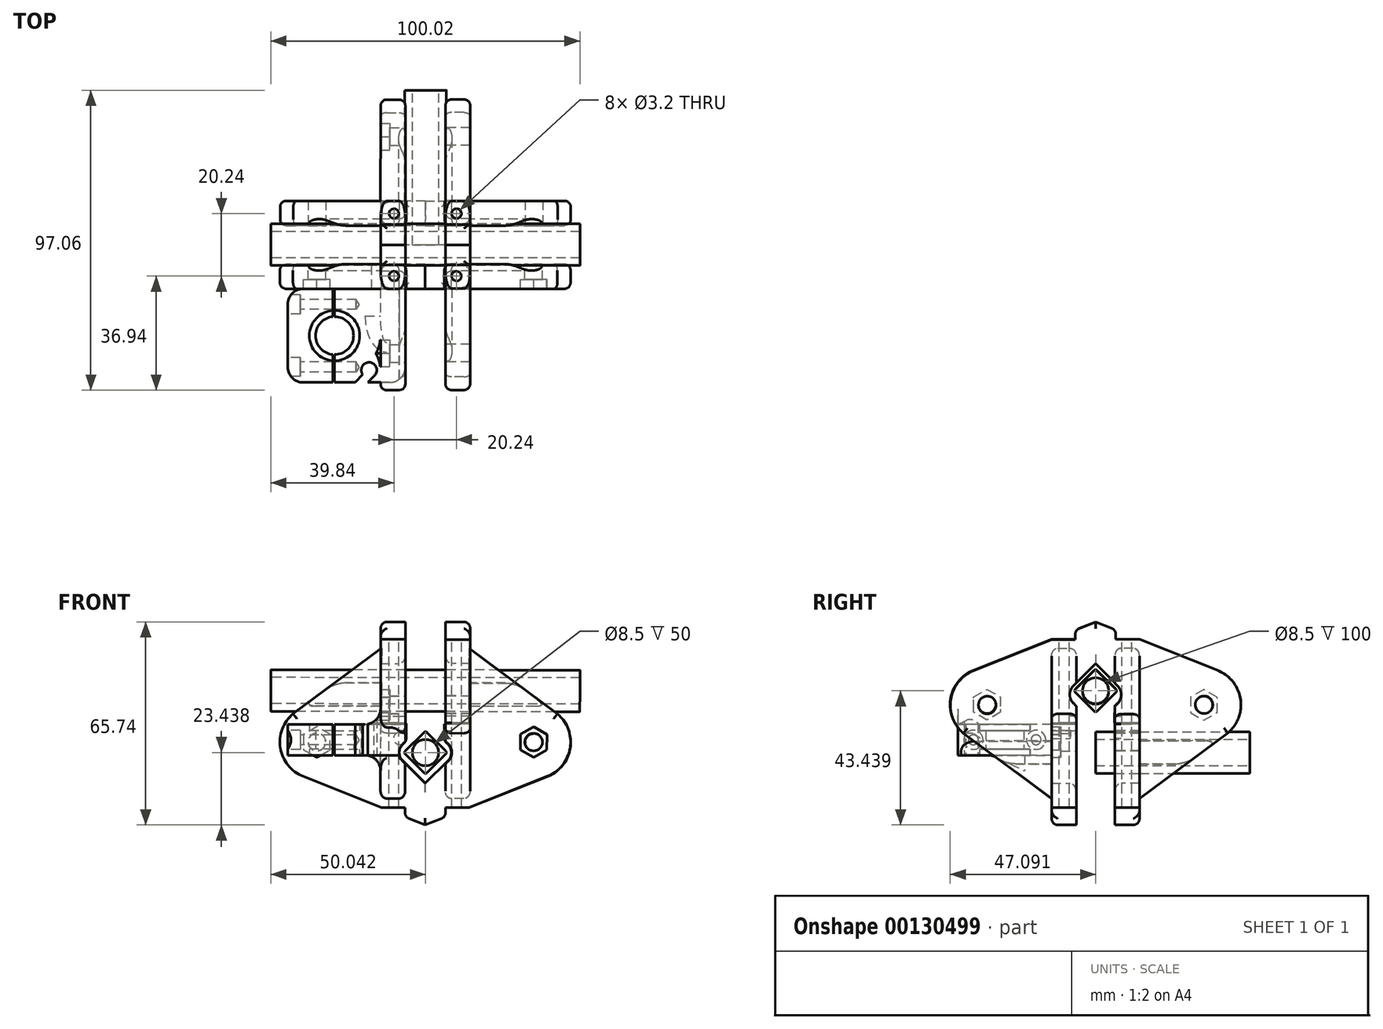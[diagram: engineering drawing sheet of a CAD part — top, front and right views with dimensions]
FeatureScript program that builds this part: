
annotation { "Feature Type Name" : "Feature", "Feature Type Description" : "" }
export const myFeature = defineFeature(function(context is Context, id is Id, definition is map)
    precondition{}
    {
        {
            assignVariable(context, id + "F0", {"name" : "wheelwidth", "anyValue" : 10.24});
        }
        {
            assignVariable(context, id + "F1", {"name" : "shimwidth", "anyValue" : 2});
        }
        {
            assignVariable(context, id + "F2", {"name" : "partwidth", "anyValue" : 8});
        }
        {
            var Q0;
            Q0=qCreatedBy(makeId("Front.planeOp"),FACE);
            var sketch = newSketch(context, id + "F3", { "sketchPlane" : qUnion([Q0])});
            skLineSegment(sketch, "E0.rect.bottom", {"start": v(6.59, -1.7) * mm, "end": v(0.65, -7.65) * mm});
            skLineSegment(sketch, "E0.rect.top", {"start": v(-0.48, 5.36) * mm, "end": v(-6.42, -0.58) * mm});
            skLineSegment(sketch, "E0.rect.left", {"start": v(6.59, -0.58) * mm, "end": v(0.65, 5.36) * mm});
            skLineSegment(sketch, "E0.rect.right", {"start": v(-0.48, -7.65) * mm, "end": v(-6.42, -1.7) * mm});
            skPoint(sketch, "E0.rect.middle", {"position": v(0.08, -1.14) * mm});
            skPoint(sketch, "E1.rect.middle", {"position": v(0.08, 18.86) * mm});
            skLineSegment(sketch, "E2", {"start": v(-6.66, 18.86) * mm, "end": v(6.82, 18.86) * mm, "construction": true});
            skCircle(sketch, "E3", {"center": v(35.08, 2.26) * mm, "radius": 11.95 * mm, "construction": true});
            skCircle(sketch, "E4", {"center": v(35.08, 2.26) * mm, "radius": 2.85 * mm});
            skCircle(sketch, "E5.cCircle", {"center": v(35.08, 2.26) * mm, "radius": 4.3 * mm, "construction": true});
            skLineSegment(sketch, "E5.0", {"start": v(39.39, 4.74) * mm, "end": v(39.38, -0.23) * mm});
            skLineSegment(sketch, "E5.1", {"start": v(39.38, -0.23) * mm, "end": v(35.08, -2.7) * mm});
            skLineSegment(sketch, "E5.2", {"start": v(35.08, -2.7) * mm, "end": v(30.78, -0.22) * mm});
            skLineSegment(sketch, "E5.3", {"start": v(30.78, -0.22) * mm, "end": v(30.79, 4.75) * mm});
            skLineSegment(sketch, "E5.4", {"start": v(30.79, 4.75) * mm, "end": v(35.09, 7.22) * mm});
            skLineSegment(sketch, "E5.5", {"start": v(35.09, 7.22) * mm, "end": v(39.39, 4.74) * mm});
            skPoint(sketch, "E6.visualSharp", {"position": v(0.08, 5.93) * mm});
            skArc(sketch, "E6.filletArc", {"start": v(0.65, 5.36) * mm, "mid": v(0.08, 5.6) * mm, "end": v(-0.48, 5.36) * mm});
            skPoint(sketch, "E7.visualSharp", {"position": v(7.15, -1.14) * mm});
            skArc(sketch, "E7.filletArc", {"start": v(6.59, -1.7) * mm, "mid": v(6.82, -1.14) * mm, "end": v(6.59, -0.58) * mm});
            skPoint(sketch, "E8.visualSharp", {"position": v(0.08, -8.21) * mm});
            skArc(sketch, "E8.filletArc", {"start": v(-0.48, -7.65) * mm, "mid": v(0.08, -7.88) * mm, "end": v(0.65, -7.65) * mm});
            skPoint(sketch, "E9.visualSharp", {"position": v(-6.99, -1.14) * mm});
            skArc(sketch, "E9.filletArc", {"start": v(-6.42, -0.58) * mm, "mid": v(-6.66, -1.14) * mm, "end": v(-6.42, -1.7) * mm});
            skLineSegment(sketch, "E10.MirrorCS", {"start": v(-0.48, 12.35) * mm, "end": v(-6.42, 18.3) * mm});
            skArc(sketch, "E11.MirrorCS", {"start": v(0.65, 12.35) * mm, "mid": v(0.08, 12.12) * mm, "end": v(-0.48, 12.35) * mm});
            skLineSegment(sketch, "E12.MirrorCS", {"start": v(6.59, 18.3) * mm, "end": v(0.65, 12.35) * mm});
            skArc(sketch, "E13.MirrorCS", {"start": v(6.59, 19.42) * mm, "mid": v(6.82, 18.86) * mm, "end": v(6.59, 18.3) * mm});
            skLineSegment(sketch, "E14.MirrorCS", {"start": v(6.59, 19.42) * mm, "end": v(0.65, 25.36) * mm});
            skLineSegment(sketch, "E15.MirrorCS", {"start": v(-0.48, 25.36) * mm, "end": v(-6.42, 19.42) * mm});
            skArc(sketch, "E16.MirrorCS", {"start": v(-0.48, 25.36) * mm, "mid": v(0.08, 25.6) * mm, "end": v(0.65, 25.36) * mm});
            skArc(sketch, "E17.MirrorCS", {"start": v(-6.42, 18.3) * mm, "mid": v(-6.66, 18.86) * mm, "end": v(-6.42, 19.42) * mm});
            skPoint(sketch, "E18.orphan", {"position": v(6.82, 18.86) * mm});
            skPoint(sketch, "E19.orphan", {"position": v(-6.66, 18.86) * mm});
            skArc(sketch, "E20", {"start": v(26.54, -1.96) * mm, "mid": v(37.25, -7.02) * mm, "end": v(44.61, 2.25) * mm});
            skCircle(sketch, "E21", {"center": v(0.08, -1.14) * mm, "radius": 4.25 * mm});
            skCircle(sketch, "E22", {"center": v(0.08, 18.86) * mm, "radius": 4.25 * mm});
            skPoint(sketch, "E23.startSnap0", {"position": v(30.78, 2.26) * mm});
            skPoint(sketch, "E24.startSnap0", {"position": v(39.38, 2.25) * mm});
            skCircle(sketch, "E25.converted", {"center": v(-34.92, 2.33) * mm, "radius": 9.53 * mm, "construction": true});
            skCircle(sketch, "E26", {"center": v(35.08, 2.26) * mm, "radius": 9.53 * mm, "construction": true});
            skLineSegment(sketch, "E27", {"start": v(-34.92, 2.33) * mm, "end": v(70.48, 2.2) * mm, "construction": true});
            skPoint(sketch, "E28", {"position": v(0.08, 8.86) * mm});
            skLineSegment(sketch, "E29", {"start": v(0, -11.12) * mm, "end": v(0, -24.58) * mm});
            skLineSegment(sketch, "E30", {"start": v(0, -24.58) * mm, "end": v(6.56, -21.97) * mm});
            skArc(sketch, "E31", {"start": v(39.5, -8.84) * mm, "mid": v(46.82, 4.5) * mm, "end": v(35.09, 14.2) * mm});
            skLineSegment(sketch, "E32", {"start": v(35.09, 14.2) * mm, "end": v(14.2, 14.2) * mm});
            skLineSegment(sketch, "E33", {"start": v(0, -11.12) * mm, "end": v(7.38, -3.74) * mm});
            skLineSegment(sketch, "E34", {"start": v(6.2, 5.93) * mm, "end": v(14.2, 5.93) * mm});
            skLineSegment(sketch, "E35", {"start": v(14.2, -18.92) * mm, "end": v(6.52, -18.92) * mm});
            skLineSegment(sketch, "E36.trimOffspring", {"start": v(14.2, -18.92) * mm, "end": v(39.5, -8.84) * mm});
            skLineSegment(sketch, "E37", {"start": v(14.2, 14.2) * mm, "end": v(14.2, 5.93) * mm});
            skLineSegment(sketch, "E38", {"start": v(0, -24.58) * mm, "end": v(0.08, 45.04) * mm, "construction": true});
            skLineSegment(sketch, "E39", {"start": v(0.08, 45.04) * mm, "end": v(35.09, 14.2) * mm, "construction": true});
            skLineSegment(sketch, "E40", {"start": v(14.2, 14.2) * mm, "end": v(14.2, 32.6) * mm});
            skLineSegment(sketch, "E41", {"start": v(14.2, 32.6) * mm, "end": v(42.8, 11.38) * mm});
            skLineSegment(sketch, "E42", {"start": v(6.2, 5.93) * mm, "end": v(6.59, -24.15) * mm, "construction": true});
            skLineSegment(sketch, "E43", {"start": v(14.2, 5.93) * mm, "end": v(14.2, -18.92) * mm, "construction": true});
            skLineSegment(sketch, "E44", {"start": v(6.56, -21.97) * mm, "end": v(6.52, -18.92) * mm});
            skPoint(sketch, "E45.visualSharp", {"position": v(9.98, -1.14) * mm});
            skArc(sketch, "E46", {"start": v(42.8, 11.38) * mm, "mid": v(30.05, 13.1) * mm, "end": v(23.13, 2.26) * mm});
            skLineSegment(sketch, "E47", {"start": v(14.2, 5.93) * mm, "end": v(14.2, 2.27) * mm});
            skLineSegment(sketch, "E48", {"start": v(14.2, 2.27) * mm, "end": v(23.13, 2.26) * mm});
            skLineSegment(sketch, "E49", {"start": v(6.2, 5.93) * mm, "end": v(6.24, 2.6) * mm});
            skLineSegment(sketch, "E50", {"start": v(6.24, 2.6) * mm, "end": v(7.38, 1.46) * mm});
            skArc(sketch, "E51", {"start": v(7.38, -3.74) * mm, "mid": v(8.46, -1.14) * mm, "end": v(7.38, 1.46) * mm});
            skLineSegment(sketch, "E52", {"start": v(0.08, 11.79) * mm, "end": v(74.95, 11.7) * mm, "construction": true});
            skLineSegment(sketch, "E53", {"start": v(14.2, 8.1) * mm, "end": v(6.2, 8.1) * mm});
            skLineSegment(sketch, "E54", {"start": v(6.2, 8.1) * mm, "end": v(6.2, 5.93) * mm});
            skSolve(sketch);
        }
        {
            var Q0;
            Q0=makeQuery(id+"F3.imprint","IMPRINT",FACE,{"disambiguationData":[TD([[makeQuery(id+"F3.imprint","IMPRINT",EDGE,{"derivedFrom":sQuery(id+"F3.wireOp",EDGE,"E5.0")}),1.0]])]});
            var Q1;
            {var subQ0=sQuery(id+"F3.wireOp",EDGE,"E32");Q1=makeQuery(id+"F3.imprint","IMPRINT",FACE,{"disambiguationData":[TD([[makeQuery(id+"F3.imprint","IMPRINT",EDGE,{"derivedFrom":subQ0}),-1.0]])]});}
            var Q2;
            {var subQ1=sQuery(id+"F3.wireOp",EDGE,"E32");Q2=makeQuery(id+"F3.imprint","IMPRINT",FACE,{"disambiguationData":[TD([[makeQuery(id+"F3.imprint","IMPRINT",EDGE,{"derivedFrom":subQ1}),1.0]])]});}
            var Q3;
            {var subQ0=sQuery(id+"F3.wireOp",EDGE,"E34");Q3=makeQuery(id+"F3.imprint","IMPRINT",FACE,{"disambiguationData":[TD([[makeQuery(id+"F3.imprint","IMPRINT",EDGE,{"derivedFrom":subQ0}),1.0]])]});}
            extrude(context, id + "F4", {"entities" : qUnion([Q0, Q1, Q2, Q3]), "depth" : (getVariable(context, 'partwidth')) * mm});
        }
        {
            var Q0;
            Q0=makeQuery(id+"F3.imprint","IMPRINT",FACE,{"disambiguationData":[TD([[makeQuery(id+"F3.imprint","IMPRINT",EDGE,{"derivedFrom":sQuery(id+"F3.wireOp",EDGE,"E4")}),-1.0]])]});
            extrude(context, id + "F5", {"entities" : qUnion([Q0]), "operationType" : NewBodyOperationType.ADD, "depth" : 5 * mm});
        }
        {
            var Q0;
            Q0=makeQuery(id+"F4.opExtrude","CAP_EDGE",EDGE,{"disambiguationData":[OSD([sQuery(id+"F3.wireOp",EDGE,"E36.trimOffspring")])],"isStart":false});
            var Q1;
            Q1=makeQuery(id+"F4.opExtrude","CAP_EDGE",EDGE,{"disambiguationData":[OSD([sQuery(id+"F3.wireOp",EDGE,"E31")])],"isStart":false});
            var Q2;
            Q2=makeQuery(id+"F4.opExtrude","CAP_EDGE",EDGE,{"disambiguationData":[OSD([sQuery(id+"F3.wireOp",EDGE,"E41")])],"isStart":false});
            var Q3;
            Q3=makeQuery(id+"F4.opExtrude","SWEPT_EDGE",EDGE,{"disambiguationData":[OSD([sQuery(id+"F3.wireOp",EDGE,"E30"),sQuery(id+"F3.wireOp",EDGE,"E44")])]});
            var Q4;
            Q4=makeQuery(id+"F4.opExtrude","CAP_EDGE",EDGE,{"disambiguationData":[OSD([sQuery(id+"F3.wireOp",EDGE,"E30")])],"isStart":false});
            var Q5;
            Q5=makeQuery(id+"F4.opExtrude","CAP_EDGE",EDGE,{"disambiguationData":[OSD([sQuery(id+"F3.wireOp",EDGE,"E33")])],"isStart":true});
            var Q6;
            Q6=makeQuery(id+"F4.opExtrude","CAP_EDGE",EDGE,{"disambiguationData":[OSD([sQuery(id+"F3.wireOp",EDGE,"E51")])],"isStart":true});
            var Q7;
            Q7=makeQuery(id+"F4.opExtrude","SWEPT_EDGE",EDGE,{"disambiguationData":[OSD([sQuery(id+"F3.wireOp",EDGE,"E49"),sQuery(id+"F3.wireOp",EDGE,"E50")])]});
            var Q8;
            Q8=makeQuery(id+"F4.opExtrude","CAP_EDGE",EDGE,{"disambiguationData":[OSD([sQuery(id+"F3.wireOp",EDGE,"E49")])],"isStart":true});
            var Q9;
            Q9=makeQuery(id+"F4.opExtrude","CAP_EDGE",EDGE,{"disambiguationData":[OSD([sQuery(id+"F3.wireOp",EDGE,"E36.trimOffspring")])],"isStart":true});
            var Q10;
            Q10=makeQuery(id+"F4.opExtrude","CAP_EDGE",EDGE,{"disambiguationData":[OSD([sQuery(id+"F3.wireOp",EDGE,"E31")])],"isStart":true});
            var Q11;
            Q11=makeQuery(id+"F4.opExtrude","CAP_EDGE",EDGE,{"disambiguationData":[OSD([sQuery(id+"F3.wireOp",EDGE,"E41")])],"isStart":true});
            var Q12;
            Q12=makeQuery(id+"F4.opExtrude","CAP_EDGE",EDGE,{"disambiguationData":[OSD([sQuery(id+"F3.wireOp",EDGE,"SLtEMFX0-vb9B-qw3r-3XGe-uKHSVcDvhUd0")])],"isStart":true});
            var Q13;
            Q13=makeQuery(id+"F4.opExtrude","CAP_EDGE",EDGE,{"disambiguationData":[OSD([sQuery(id+"F3.wireOp",EDGE,"E54")])],"isStart":true});
            fillet(context, id + "F6", {"entities" : qUnion([Q0, Q1, Q2, Q3, Q4, Q5, Q6, Q7, Q8, Q9, Q10, Q11, Q12, Q13]), "radius" : (getVariable(context, 'partwidth') / 4) * mm, "tangentPropagation" : true, "allowEdgeOverflow" : false});
        }
        {
            var Q0;
            Q0=makeQuery(id+"F4.opExtrude","SWEPT_BODY",BODY,{"disambiguationData":[OSD([sQuery(id+"F3.wireOp",EDGE,"E5.0"),sQuery(id+"F3.wireOp",EDGE,"E5.1"),sQuery(id+"F3.wireOp",EDGE,"E5.2"),sQuery(id+"F3.wireOp",EDGE,"E5.3"),sQuery(id+"F3.wireOp",EDGE,"E5.4"),sQuery(id+"F3.wireOp",EDGE,"E5.5"),sQuery(id+"F3.wireOp",EDGE,"E29"),sQuery(id+"F3.wireOp",EDGE,"E30"),sQuery(id+"F3.wireOp",EDGE,"E31"),sQuery(id+"F3.wireOp",EDGE,"E32"),sQuery(id+"F3.wireOp",EDGE,"mdJr3x9G-8PZe-KLZ4-2jMX-8YXO7VhJZwa1"),sQuery(id+"F3.wireOp",EDGE,"E33"),sQuery(id+"F3.wireOp",EDGE,"HpUcd2lR-hpQP-pT3M-pNBS-jOqEvMcl2bwM"),sQuery(id+"F3.wireOp",EDGE,"E34"),sQuery(id+"F3.wireOp",EDGE,"Nq46po5O-rSWg-Le1q-s3LO-EsxNW4JDjgbP"),sQuery(id+"F3.wireOp",EDGE,"E35"),sQuery(id+"F3.wireOp",EDGE,"UB4Qnz5i-1XTo-EqLd-Vyfx-Gw4a37x92uXC"),sQuery(id+"F3.wireOp",EDGE,"E36.trimOffspring")])]});
            var Q1;
            Q1=qCreatedBy(makeId("Right.planeOp"),FACE);
            mirror(context, id + "F7", {"operationType" : NewBodyOperationType.ADD, "entities" : qUnion([Q0]), "mirrorPlane" : qUnion([Q1])});
        }
        {
            var Q0;
            Q0=qCreatedBy(makeId("Right.planeOp"),FACE);
            var sketch = newSketch(context, id + "F8", { "sketchPlane" : qUnion([Q0])});
            skLineSegment(sketch, "E55", {"start": v(0, 27.69) * mm, "end": v(-7.18, 20.45) * mm});
            skLineSegment(sketch, "E56", {"start": v(-7.15, 14.8) * mm, "end": v(0, 7.7) * mm});
            skLineSegment(sketch, "E57", {"start": v(0, 7.7) * mm, "end": v(7.18, 14.94) * mm});
            skLineSegment(sketch, "E58", {"start": v(7.15, 20.6) * mm, "end": v(0, 27.69) * mm});
            skPoint(sketch, "E59.visualSharp", {"position": v(-10, 17.6) * mm});
            skArc(sketch, "E59.filletArc", {"start": v(-7.18, 20.45) * mm, "mid": v(-8.33, 17.61) * mm, "end": v(-7.15, 14.8) * mm});
            skPoint(sketch, "E60.visualSharp", {"position": v(10, 17.78) * mm});
            skArc(sketch, "E60.filletArc", {"start": v(7.18, 14.94) * mm, "mid": v(8.33, 17.77) * mm, "end": v(7.15, 20.6) * mm});
            skSolve(sketch);
        }
        {
            var Q0;
            Q0=makeQuery(id+"F4.opExtrude","SWEPT_BODY",BODY,{"disambiguationData":[OSD([sQuery(id+"F3.wireOp",EDGE,"E5.0"),sQuery(id+"F3.wireOp",EDGE,"E5.1"),sQuery(id+"F3.wireOp",EDGE,"E5.2"),sQuery(id+"F3.wireOp",EDGE,"E5.3"),sQuery(id+"F3.wireOp",EDGE,"E5.4"),sQuery(id+"F3.wireOp",EDGE,"E5.5"),sQuery(id+"F3.wireOp",EDGE,"E29"),sQuery(id+"F3.wireOp",EDGE,"E30"),sQuery(id+"F3.wireOp",EDGE,"E31"),sQuery(id+"F3.wireOp",EDGE,"E32"),sQuery(id+"F3.wireOp",EDGE,"mdJr3x9G-8PZe-KLZ4-2jMX-8YXO7VhJZwa1"),sQuery(id+"F3.wireOp",EDGE,"E33"),sQuery(id+"F3.wireOp",EDGE,"HpUcd2lR-hpQP-pT3M-pNBS-jOqEvMcl2bwM"),sQuery(id+"F3.wireOp",EDGE,"E34"),sQuery(id+"F3.wireOp",EDGE,"Nq46po5O-rSWg-Le1q-s3LO-EsxNW4JDjgbP"),sQuery(id+"F3.wireOp",EDGE,"E35"),sQuery(id+"F3.wireOp",EDGE,"UB4Qnz5i-1XTo-EqLd-Vyfx-Gw4a37x92uXC"),sQuery(id+"F3.wireOp",EDGE,"E36.trimOffspring")])]});
            var Q1;
            Q1=makeQuery(id+"F18.opPattern","COPY",BODY,{"derivedFrom":makeQuery(id+"F4.opExtrude","SWEPT_BODY",BODY,{"disambiguationData":[OSD([sQuery(id+"F3.wireOp",EDGE,"E5.0"),sQuery(id+"F3.wireOp",EDGE,"E5.1"),sQuery(id+"F3.wireOp",EDGE,"E5.2"),sQuery(id+"F3.wireOp",EDGE,"E5.3"),sQuery(id+"F3.wireOp",EDGE,"E5.4"),sQuery(id+"F3.wireOp",EDGE,"E5.5"),sQuery(id+"F3.wireOp",EDGE,"E29"),sQuery(id+"F3.wireOp",EDGE,"E30"),sQuery(id+"F3.wireOp",EDGE,"E31"),sQuery(id+"F3.wireOp",EDGE,"E32"),sQuery(id+"F3.wireOp",EDGE,"mdJr3x9G-8PZe-KLZ4-2jMX-8YXO7VhJZwa1"),sQuery(id+"F3.wireOp",EDGE,"E33"),sQuery(id+"F3.wireOp",EDGE,"HpUcd2lR-hpQP-pT3M-pNBS-jOqEvMcl2bwM"),sQuery(id+"F3.wireOp",EDGE,"E34"),sQuery(id+"F3.wireOp",EDGE,"Nq46po5O-rSWg-Le1q-s3LO-EsxNW4JDjgbP"),sQuery(id+"F3.wireOp",EDGE,"E35"),sQuery(id+"F3.wireOp",EDGE,"UB4Qnz5i-1XTo-EqLd-Vyfx-Gw4a37x92uXC"),sQuery(id+"F3.wireOp",EDGE,"E36.trimOffspring")])]}),"instanceName":"1"});
            var Q2;
            Q2=qCreatedBy(makeId("Front.planeOp"),FACE);
            transform(context, id + "F9", {"entities" : qUnion([Q0, Q1]), "transformType" : TransformType.TRANSLATION_DISTANCE, "transformDirection" : qUnion([Q2]), "distance" : -((getVariable(context, 'partwidth') / 2) - (getVariable(context, 'wheelwidth'))) * mm, "makeCopy" : false});
        }
        {
            var Q0;
            Q0=makeQuery(id+"F8.imprint","IMPRINT",FACE,{"disambiguationData":[TD([[makeQuery(id+"F8.imprint","IMPRINT",EDGE,{"derivedFrom":sQuery(id+"F8.wireOp",EDGE,"E55")}),1.0]])]});
            extrude(context, id + "F10", {"entities" : qUnion([Q0]), "operationType" : NewBodyOperationType.REMOVE, "oppositeDirection" : true, "depth" : 50 * mm, "hasSecondDirection" : true, "secondDirectionOppositeDirection" : false, "secondDirectionDepth" : 50 * mm});
        }
        {
            var Q0;
            Q0=makeQuery(id+"F4.opExtrude","SWEPT_BODY",BODY,{"disambiguationData":[OSD([sQuery(id+"F3.wireOp",EDGE,"E5.0"),sQuery(id+"F3.wireOp",EDGE,"E5.1"),sQuery(id+"F3.wireOp",EDGE,"E5.2"),sQuery(id+"F3.wireOp",EDGE,"E5.3"),sQuery(id+"F3.wireOp",EDGE,"E5.4"),sQuery(id+"F3.wireOp",EDGE,"E5.5"),sQuery(id+"F3.wireOp",EDGE,"E29"),sQuery(id+"F3.wireOp",EDGE,"E30"),sQuery(id+"F3.wireOp",EDGE,"E31"),sQuery(id+"F3.wireOp",EDGE,"E32"),sQuery(id+"F3.wireOp",EDGE,"mdJr3x9G-8PZe-KLZ4-2jMX-8YXO7VhJZwa1"),sQuery(id+"F3.wireOp",EDGE,"E33"),sQuery(id+"F3.wireOp",EDGE,"HpUcd2lR-hpQP-pT3M-pNBS-jOqEvMcl2bwM"),sQuery(id+"F3.wireOp",EDGE,"E34"),sQuery(id+"F3.wireOp",EDGE,"Nq46po5O-rSWg-Le1q-s3LO-EsxNW4JDjgbP"),sQuery(id+"F3.wireOp",EDGE,"E35"),sQuery(id+"F3.wireOp",EDGE,"UB4Qnz5i-1XTo-EqLd-Vyfx-Gw4a37x92uXC"),sQuery(id+"F3.wireOp",EDGE,"E36.trimOffspring")])]});
            var Q1;
            Q1=sQuery(id+"F3.wireOp",EDGE,"E38");
            transform(context, id + "F11", {"entities" : qUnion([Q0]), "transformType" : TransformType.ROTATION, "transformAxis" : qUnion([Q1]), "angle" : 90 * degree, "oppositeDirection" : true, "makeCopy" : true});
        }
        {
            var Q0;
            Q0=makeQuery(id+"F11.opPattern","COPY",BODY,{"derivedFrom":makeQuery(id+"F4.opExtrude","SWEPT_BODY",BODY,{"disambiguationData":[OSD([sQuery(id+"F3.wireOp",EDGE,"E5.0"),sQuery(id+"F3.wireOp",EDGE,"E5.1"),sQuery(id+"F3.wireOp",EDGE,"E5.2"),sQuery(id+"F3.wireOp",EDGE,"E5.3"),sQuery(id+"F3.wireOp",EDGE,"E5.4"),sQuery(id+"F3.wireOp",EDGE,"E5.5"),sQuery(id+"F3.wireOp",EDGE,"E29"),sQuery(id+"F3.wireOp",EDGE,"E30"),sQuery(id+"F3.wireOp",EDGE,"E31"),sQuery(id+"F3.wireOp",EDGE,"E32"),sQuery(id+"F3.wireOp",EDGE,"mdJr3x9G-8PZe-KLZ4-2jMX-8YXO7VhJZwa1"),sQuery(id+"F3.wireOp",EDGE,"E33"),sQuery(id+"F3.wireOp",EDGE,"HpUcd2lR-hpQP-pT3M-pNBS-jOqEvMcl2bwM"),sQuery(id+"F3.wireOp",EDGE,"E34"),sQuery(id+"F3.wireOp",EDGE,"Nq46po5O-rSWg-Le1q-s3LO-EsxNW4JDjgbP"),sQuery(id+"F3.wireOp",EDGE,"E35"),sQuery(id+"F3.wireOp",EDGE,"UB4Qnz5i-1XTo-EqLd-Vyfx-Gw4a37x92uXC"),sQuery(id+"F3.wireOp",EDGE,"E36.trimOffspring")])]}),"instanceName":"1"});
            var Q1;
            Q1=sQuery(id+"F3.wireOp",EDGE,"E27");
            transform(context, id + "F12", {"entities" : qUnion([Q0]), "transformType" : TransformType.ROTATION, "transformAxis" : qUnion([Q1]), "angle" : 180 * degree, "makeCopy" : false});
        }
        {
            var Q0;
            Q0=makeQuery(id+"FKIDPC5YcO8KzMp_1.opPattern","COPY",BODY,{"derivedFrom":makeQuery(id+"F11.opPattern","COPY",BODY,{"derivedFrom":makeQuery(id+"F4.opExtrude","SWEPT_BODY",BODY,{"disambiguationData":[OSD([sQuery(id+"F3.wireOp",EDGE,"E5.0"),sQuery(id+"F3.wireOp",EDGE,"E5.1"),sQuery(id+"F3.wireOp",EDGE,"E5.2"),sQuery(id+"F3.wireOp",EDGE,"E5.3"),sQuery(id+"F3.wireOp",EDGE,"E5.4"),sQuery(id+"F3.wireOp",EDGE,"E5.5"),sQuery(id+"F3.wireOp",EDGE,"E29"),sQuery(id+"F3.wireOp",EDGE,"E30"),sQuery(id+"F3.wireOp",EDGE,"E31"),sQuery(id+"F3.wireOp",EDGE,"E32"),sQuery(id+"F3.wireOp",EDGE,"E33"),sQuery(id+"F3.wireOp",EDGE,"E34"),sQuery(id+"F3.wireOp",EDGE,"E35"),sQuery(id+"F3.wireOp",EDGE,"UB4Qnz5i-1XTo-EqLd-Vyfx-Gw4a37x92uXC"),sQuery(id+"F3.wireOp",EDGE,"E36.trimOffspring"),sQuery(id+"F3.wireOp",EDGE,"g6woaz09-jX6f-EFWg-c65b-02BoFioKR391"),sQuery(id+"F3.wireOp",EDGE,"E37")])]}),"instanceName":"1"}),"instanceName":"1"});
            var Q1;
            Q1=makeQuery(id+"F11.opPattern","COPY",BODY,{"derivedFrom":makeQuery(id+"F4.opExtrude","SWEPT_BODY",BODY,{"disambiguationData":[OSD([sQuery(id+"F3.wireOp",EDGE,"E5.0"),sQuery(id+"F3.wireOp",EDGE,"E5.1"),sQuery(id+"F3.wireOp",EDGE,"E5.2"),sQuery(id+"F3.wireOp",EDGE,"E5.3"),sQuery(id+"F3.wireOp",EDGE,"E5.4"),sQuery(id+"F3.wireOp",EDGE,"E5.5"),sQuery(id+"F3.wireOp",EDGE,"E29"),sQuery(id+"F3.wireOp",EDGE,"E30"),sQuery(id+"F3.wireOp",EDGE,"E31"),sQuery(id+"F3.wireOp",EDGE,"E32"),sQuery(id+"F3.wireOp",EDGE,"E33"),sQuery(id+"F3.wireOp",EDGE,"E34"),sQuery(id+"F3.wireOp",EDGE,"E35"),sQuery(id+"F3.wireOp",EDGE,"UB4Qnz5i-1XTo-EqLd-Vyfx-Gw4a37x92uXC"),sQuery(id+"F3.wireOp",EDGE,"E36.trimOffspring"),sQuery(id+"F3.wireOp",EDGE,"g6woaz09-jX6f-EFWg-c65b-02BoFioKR391"),sQuery(id+"F3.wireOp",EDGE,"E37")])]}),"instanceName":"1"});
            transform(context, id + "F13", {"entities" : qUnion([Q0, Q1]), "transformType" : TransformType.TRANSLATION_3D, "dx" : 0 * mm, "dy" : 0 * mm, "dz" : 12 * mm, "makeCopy" : false});
        }
        {
            var Q0;
            Q0=makeQuery(id+"F11.opPattern","COPY",BODY,{"derivedFrom":makeQuery(id+"F4.opExtrude","SWEPT_BODY",BODY,{"disambiguationData":[OSD([sQuery(id+"F3.wireOp",EDGE,"E5.0"),sQuery(id+"F3.wireOp",EDGE,"E5.1"),sQuery(id+"F3.wireOp",EDGE,"E5.2"),sQuery(id+"F3.wireOp",EDGE,"E5.3"),sQuery(id+"F3.wireOp",EDGE,"E5.4"),sQuery(id+"F3.wireOp",EDGE,"E5.5"),sQuery(id+"F3.wireOp",EDGE,"E29"),sQuery(id+"F3.wireOp",EDGE,"E30"),sQuery(id+"F3.wireOp",EDGE,"E31"),sQuery(id+"F3.wireOp",EDGE,"E32"),sQuery(id+"F3.wireOp",EDGE,"mdJr3x9G-8PZe-KLZ4-2jMX-8YXO7VhJZwa1"),sQuery(id+"F3.wireOp",EDGE,"E33"),sQuery(id+"F3.wireOp",EDGE,"HpUcd2lR-hpQP-pT3M-pNBS-jOqEvMcl2bwM"),sQuery(id+"F3.wireOp",EDGE,"E34"),sQuery(id+"F3.wireOp",EDGE,"Nq46po5O-rSWg-Le1q-s3LO-EsxNW4JDjgbP"),sQuery(id+"F3.wireOp",EDGE,"E35"),sQuery(id+"F3.wireOp",EDGE,"UB4Qnz5i-1XTo-EqLd-Vyfx-Gw4a37x92uXC"),sQuery(id+"F3.wireOp",EDGE,"E36.trimOffspring")])]}),"instanceName":"1"});
            var Q1;
            Q1=sQuery(id+"F3.wireOp",EDGE,"E27");
            transform(context, id + "F14", {"entities" : qUnion([Q0]), "transformType" : TransformType.TRANSLATION_DISTANCE, "transformDirection" : qUnion([Q1]), "distance" : (-(getVariable(context, 'partwidth')) + (getVariable(context, 'wheelwidth')) - getVariable(context, 'shimwidth')) * mm, "oppositeDirection" : true, "makeCopy" : false});
        }
        {
            var Q0;
            Q0=qCreatedBy(makeId("Front.planeOp"),FACE);
            var sketch = newSketch(context, id + "F15", { "sketchPlane" : qUnion([Q0])});
            skLineSegment(sketch, "E61", {"start": v(0, 13.56) * mm, "end": v(-26.7, -18.9) * mm});
            skLineSegment(sketch, "E62", {"start": v(-26.7, -18.9) * mm, "end": v(26.7, -18.9) * mm});
            skLineSegment(sketch, "E63", {"start": v(26.7, -18.9) * mm, "end": v(0, 13.56) * mm});
            skLineSegment(sketch, "E64", {"start": v(0, 13.56) * mm, "end": v(0, -18.9) * mm, "construction": true});
            skLineSegment(sketch, "E65.0", {"start": v(0, -13.95) * mm, "end": v(-8.8, -5.15) * mm});
            skArc(sketch, "E65.1", {"start": v(-8.8, -5.15) * mm, "mid": v(-10.46, -1.14) * mm, "end": v(-8.8, 2.87) * mm});
            skLineSegment(sketch, "E65.2", {"start": v(0, -13.95) * mm, "end": v(8.8, -5.15) * mm});
            skArc(sketch, "E65.3", {"start": v(8.8, -5.15) * mm, "mid": v(10.46, -1.14) * mm, "end": v(8.8, 2.87) * mm});
            skLineSegment(sketch, "E66.0", {"start": v(-7.38, -3.74) * mm, "end": v(0, -11.12) * mm});
            skArc(sketch, "E66.1", {"start": v(-7.38, 1.46) * mm, "mid": v(-8.46, -1.14) * mm, "end": v(-7.38, -3.74) * mm});
            skArc(sketch, "E66.2", {"start": v(7.38, 1.46) * mm, "mid": v(8.46, -1.14) * mm, "end": v(7.38, -3.74) * mm});
            skLineSegment(sketch, "E66.3", {"start": v(-6.82, 2.02) * mm, "end": v(-7.38, 1.46) * mm});
            skLineSegment(sketch, "E66.4", {"start": v(7.38, -3.74) * mm, "end": v(0, -11.12) * mm});
            skLineSegment(sketch, "E66.5", {"start": v(6.82, 2.02) * mm, "end": v(7.38, 1.46) * mm});
            skArc(sketch, "E66.6", {"start": v(6.82, 2.02) * mm, "mid": v(6.4, 2.66) * mm, "end": v(6.23, 3.4) * mm});
            skArc(sketch, "E66.7", {"start": v(-6.82, 2.02) * mm, "mid": v(-6.4, 2.66) * mm, "end": v(-6.23, 3.4) * mm});
            skLineSegment(sketch, "E67", {"start": v(-6.23, 3.4) * mm, "end": v(-6.23, 5.99) * mm});
            skLineSegment(sketch, "E68", {"start": v(-6.23, 5.99) * mm, "end": v(6.23, 5.99) * mm});
            skLineSegment(sketch, "E69", {"start": v(6.23, 5.99) * mm, "end": v(6.23, 3.4) * mm});
            skSolve(sketch);
        }
        {
            var Q0;
            Q0=makeQuery(id+"F3.imprint","IMPRINT",FACE,{"disambiguationData":[TD([[makeQuery(id+"F3.imprint","IMPRINT",EDGE,{"derivedFrom":sQuery(id+"F3.wireOp",EDGE,"E0.rect.bottom")}),-1.0]])]});
            extrude(context, id + "F16", {"entities" : qUnion([Q0]), "depth" : 50 * mm, "hasSecondDirection" : true, "secondDirectionOppositeDirection" : true, "secondDirectionDepth" : 50 * mm});
        }
        {
            var Q0;
            Q0=makeQuery(id+"F4.opExtrude","SWEPT_BODY",BODY,{"disambiguationData":[OSD([sQuery(id+"F3.wireOp",EDGE,"E5.0"),sQuery(id+"F3.wireOp",EDGE,"E5.1"),sQuery(id+"F3.wireOp",EDGE,"E5.2"),sQuery(id+"F3.wireOp",EDGE,"E5.3"),sQuery(id+"F3.wireOp",EDGE,"E5.4"),sQuery(id+"F3.wireOp",EDGE,"E5.5"),sQuery(id+"F3.wireOp",EDGE,"E29"),sQuery(id+"F3.wireOp",EDGE,"E30"),sQuery(id+"F3.wireOp",EDGE,"E31"),sQuery(id+"F3.wireOp",EDGE,"E33"),sQuery(id+"F3.wireOp",EDGE,"E34"),sQuery(id+"F3.wireOp",EDGE,"E35"),sQuery(id+"F3.wireOp",EDGE,"UB4Qnz5i-1XTo-EqLd-Vyfx-Gw4a37x92uXC"),sQuery(id+"F3.wireOp",EDGE,"E36.trimOffspring"),sQuery(id+"F3.wireOp",EDGE,"g6woaz09-jX6f-EFWg-c65b-02BoFioKR391"),sQuery(id+"F3.wireOp",EDGE,"E37"),sQuery(id+"F3.wireOp",EDGE,"E40"),sQuery(id+"F3.wireOp",EDGE,"E41")])]});
            var Q1;
            Q1=sQuery(id+"F3.wireOp",EDGE,"E38");
            transform(context, id + "F17", {"entities" : qUnion([Q0]), "transformType" : TransformType.ROTATION, "transformAxis" : qUnion([Q1]), "angle" : 180 * degree, "makeCopy" : true});
        }
        {
            var Q0;
            Q0=makeQuery(id+"F4.opExtrude","SWEPT_BODY",BODY,{"disambiguationData":[OSD([sQuery(id+"F3.wireOp",EDGE,"E5.0"),sQuery(id+"F3.wireOp",EDGE,"E5.1"),sQuery(id+"F3.wireOp",EDGE,"E5.2"),sQuery(id+"F3.wireOp",EDGE,"E5.3"),sQuery(id+"F3.wireOp",EDGE,"E5.4"),sQuery(id+"F3.wireOp",EDGE,"E5.5"),sQuery(id+"F3.wireOp",EDGE,"E29"),sQuery(id+"F3.wireOp",EDGE,"E30"),sQuery(id+"F3.wireOp",EDGE,"E31"),sQuery(id+"F3.wireOp",EDGE,"E32"),sQuery(id+"F3.wireOp",EDGE,"mdJr3x9G-8PZe-KLZ4-2jMX-8YXO7VhJZwa1"),sQuery(id+"F3.wireOp",EDGE,"E33"),sQuery(id+"F3.wireOp",EDGE,"HpUcd2lR-hpQP-pT3M-pNBS-jOqEvMcl2bwM"),sQuery(id+"F3.wireOp",EDGE,"E34"),sQuery(id+"F3.wireOp",EDGE,"Nq46po5O-rSWg-Le1q-s3LO-EsxNW4JDjgbP"),sQuery(id+"F3.wireOp",EDGE,"E35"),sQuery(id+"F3.wireOp",EDGE,"UB4Qnz5i-1XTo-EqLd-Vyfx-Gw4a37x92uXC"),sQuery(id+"F3.wireOp",EDGE,"E36.trimOffspring")])]});
            var Q1;
            {var subQ0=makeQuery(id+"F4.opExtrude","SWEPT_EDGE",EDGE,{"disambiguationData":[OSD([sQuery(id+"F3.wireOp",EDGE,"E29"),sQuery(id+"F3.wireOp",EDGE,"E30")])]});Q1=makeQuery(id+"F7.boolean.opBoolean","MERGE",EDGE,{"derivedFrom":[subQ0,makeQuery(id+"F7.opPattern","COPY",EDGE,{"derivedFrom":subQ0,"instanceName":"1"})]});}
            transform(context, id + "F18", {"entities" : qUnion([Q0]), "transformType" : TransformType.TRANSLATION_DISTANCE, "transformDirection" : qUnion([Q1]), "distance" : (getVariable(context, 'partwidth') + getVariable(context, 'wheelwidth') + (2 * getVariable(context, 'shimwidth'))) * mm, "makeCopy" : true});
        }
        {
            var Q0;
            Q0=makeQuery(id+"F18.opPattern","COPY",BODY,{"derivedFrom":makeQuery(id+"F4.opExtrude","SWEPT_BODY",BODY,{"disambiguationData":[OSD([sQuery(id+"F3.wireOp",EDGE,"E5.0"),sQuery(id+"F3.wireOp",EDGE,"E5.1"),sQuery(id+"F3.wireOp",EDGE,"E5.2"),sQuery(id+"F3.wireOp",EDGE,"E5.3"),sQuery(id+"F3.wireOp",EDGE,"E5.4"),sQuery(id+"F3.wireOp",EDGE,"E5.5"),sQuery(id+"F3.wireOp",EDGE,"E29"),sQuery(id+"F3.wireOp",EDGE,"E30"),sQuery(id+"F3.wireOp",EDGE,"E31"),sQuery(id+"F3.wireOp",EDGE,"E33"),sQuery(id+"F3.wireOp",EDGE,"E34"),sQuery(id+"F3.wireOp",EDGE,"E35"),sQuery(id+"F3.wireOp",EDGE,"UB4Qnz5i-1XTo-EqLd-Vyfx-Gw4a37x92uXC"),sQuery(id+"F3.wireOp",EDGE,"E36.trimOffspring"),sQuery(id+"F3.wireOp",EDGE,"g6woaz09-jX6f-EFWg-c65b-02BoFioKR391"),sQuery(id+"F3.wireOp",EDGE,"E37"),sQuery(id+"F3.wireOp",EDGE,"E40"),sQuery(id+"F3.wireOp",EDGE,"E41")])]}),"instanceName":"1"});
            deleteBodies(context, id + "F19", {"entities" : qUnion([Q0])});
        }
        {
            var Q0;
            Q0=makeQuery(id+"F11.opPattern","COPY",BODY,{"derivedFrom":makeQuery(id+"F4.opExtrude","SWEPT_BODY",BODY,{"disambiguationData":[OSD([sQuery(id+"F3.wireOp",EDGE,"E5.0"),sQuery(id+"F3.wireOp",EDGE,"E5.1"),sQuery(id+"F3.wireOp",EDGE,"E5.2"),sQuery(id+"F3.wireOp",EDGE,"E5.3"),sQuery(id+"F3.wireOp",EDGE,"E5.4"),sQuery(id+"F3.wireOp",EDGE,"E5.5"),sQuery(id+"F3.wireOp",EDGE,"E29"),sQuery(id+"F3.wireOp",EDGE,"E30"),sQuery(id+"F3.wireOp",EDGE,"E31"),sQuery(id+"F3.wireOp",EDGE,"E33"),sQuery(id+"F3.wireOp",EDGE,"E34"),sQuery(id+"F3.wireOp",EDGE,"E35"),sQuery(id+"F3.wireOp",EDGE,"E36.trimOffspring"),sQuery(id+"F3.wireOp",EDGE,"g6woaz09-jX6f-EFWg-c65b-02BoFioKR391"),sQuery(id+"F3.wireOp",EDGE,"E37"),sQuery(id+"F3.wireOp",EDGE,"E40"),sQuery(id+"F3.wireOp",EDGE,"E41"),sQuery(id+"F3.wireOp",EDGE,"E44"),sQuery(id+"F3.wireOp",EDGE,"E45.filletArc")])]}),"instanceName":"1"});
            var Q1;
            Q1=sQuery(id+"F3.wireOp",EDGE,"E38");
            transform(context, id + "F20", {"entities" : qUnion([Q0]), "transformType" : TransformType.ROTATION, "transformAxis" : qUnion([Q1]), "angle" : 180 * degree, "makeCopy" : true});
        }
        {
            var Q0;
            Q0=qCreatedBy(makeId("Top.planeOp"),FACE);
            var sketch = newSketch(context, id + "F21", { "sketchPlane" : qUnion([Q0])});
            skPoint(sketch, "E70.middle", {"position": v(0, 0) * mm});
            skLineSegment(sketch, "E71", {"start": v(0, 16.2) * mm, "end": v(0, -11.97) * mm, "construction": true});
            skLineSegment(sketch, "E72", {"start": v(-15.84, 10.12) * mm, "end": v(17.3, 10.12) * mm, "construction": true});
            skLineSegment(sketch, "E73", {"start": v(-10.12, 15.82) * mm, "end": v(-10.12, -16.96) * mm, "construction": true});
            skLineSegment(sketch, "E74.MirrorCS", {"start": v(10.12, 15.82) * mm, "end": v(10.12, -16.96) * mm, "construction": true});
            skCircle(sketch, "E75", {"center": v(-10.12, 10.12) * mm, "radius": 1.6 * mm});
            skCircle(sketch, "E76.0.1.0", {"center": v(-10.12, -10.12) * mm, "radius": 1.6 * mm});
            skCircle(sketch, "E76.1.0.0", {"center": v(10.12, 10.12) * mm, "radius": 1.6 * mm});
            skCircle(sketch, "E76.1.1.0", {"center": v(10.12, -10.12) * mm, "radius": 1.6 * mm});
            skLineSegment(sketch, "E76.direction1", {"start": v(-10.12, 10.12) * mm, "end": v(10.12, 10.12) * mm, "construction": true});
            skLineSegment(sketch, "E76.direction2", {"start": v(-10.12, 10.12) * mm, "end": v(-10.12, -10.12) * mm, "construction": true});
            skSolve(sketch);
        }
        {
            var Q0;
            Q0 = qSketchRegion(id + "F21", true);
            extrude(context, id + "F22", {"entities" : qUnion([Q0]), "operationType" : NewBodyOperationType.REMOVE, "oppositeDirection" : true, "depth" : 100 * mm, "hasSecondDirection" : true, "secondDirectionOppositeDirection" : false, "secondDirectionDepth" : 100 * mm});
        }
        {
            var Q0;
            Q0=makeQuery(id+"F3.imprint","IMPRINT",FACE,{"disambiguationData":[TD([[makeQuery(id+"F3.imprint","IMPRINT",EDGE,{"derivedFrom":sQuery(id+"F3.wireOp",EDGE,"E10.MirrorCS")}),-1.0]])]});
            extrude(context, id + "F23", {"entities" : qUnion([Q0]), "depth" : 50 * mm, "hasSecondDirection" : true, "secondDirectionOppositeDirection" : true, "secondDirectionDepth" : 50 * mm});
        }
        {
            var Q0;
            Q0=makeQuery(id+"F23.opExtrude","SWEPT_BODY",BODY,{"disambiguationData":[OSD([sQuery(id+"F3.wireOp",EDGE,"E10.MirrorCS"),sQuery(id+"F3.wireOp",EDGE,"E11.MirrorCS"),sQuery(id+"F3.wireOp",EDGE,"E12.MirrorCS"),sQuery(id+"F3.wireOp",EDGE,"E13.MirrorCS"),sQuery(id+"F3.wireOp",EDGE,"E14.MirrorCS"),sQuery(id+"F3.wireOp",EDGE,"E15.MirrorCS"),sQuery(id+"F3.wireOp",EDGE,"E16.MirrorCS"),sQuery(id+"F3.wireOp",EDGE,"E17.MirrorCS"),sQuery(id+"F3.wireOp",EDGE,"E22")])]});
            var Q1;
            Q1=sQuery(id+"F3.wireOp",EDGE,"E38");
            transform(context, id + "F24", {"entities" : qUnion([Q0]), "transformType" : TransformType.ROTATION, "transformAxis" : qUnion([Q1]), "angle" : 90 * degree, "makeCopy" : false});
        }
        {
            var Q0;
            Q0=qCreatedBy(makeId("Top.planeOp"),FACE);
            var sketch = newSketch(context, id + "F25", { "sketchPlane" : qUnion([Q0])});
            skLineSegment(sketch, "E77", {"start": v(-14.2, -14.24) * mm, "end": v(-49.02, -49.06) * mm, "construction": true});
            skCircle(sketch, "E78", {"center": v(-29.35, -29.4) * mm, "radius": 8.15 * mm});
            skLineSegment(sketch, "E79", {"start": v(-46, -18.24) * mm, "end": v(-5.1, -18.24) * mm, "construction": true});
            skLineSegment(sketch, "E80", {"start": v(-18.2, -7.11) * mm, "end": v(-18.2, -48.36) * mm, "construction": true});
            skLineSegment(sketch, "E81", {"start": v(-48.3, -14.24) * mm, "end": v(1.04, -14.24) * mm, "construction": true});
            skLineSegment(sketch, "E82", {"start": v(-14.2, -48.92) * mm, "end": v(-14.2, -8.68) * mm, "construction": true});
            skLineSegment(sketch, "E83", {"start": v(-40.5, -3.7) * mm, "end": v(-40.5, -49.45) * mm, "construction": true});
            skLineSegment(sketch, "E84", {"start": v(-2.29, -40.54) * mm, "end": v(-52.68, -40.54) * mm, "construction": true});
            skLineSegment(sketch, "E85", {"start": v(-44.5, -3.24) * mm, "end": v(-44.5, -52.1) * mm, "construction": true});
            skLineSegment(sketch, "E86", {"start": v(-56.3, -44.54) * mm, "end": v(-6.47, -44.54) * mm, "construction": true});
            skCircle(sketch, "E87", {"center": v(-18.2, -40.54) * mm, "radius": 2.5 * mm, "construction": true});
            skLineSegment(sketch, "E88", {"start": v(-20.25, -41.97) * mm, "end": v(-29.19, -51.58) * mm, "construction": true});
            skLineSegment(sketch, "E89", {"start": v(-29.19, -51.58) * mm, "end": v(-27, -53.62) * mm, "construction": true});
            skLineSegment(sketch, "E90", {"start": v(-27, -53.62) * mm, "end": v(-16.65, -42.5) * mm, "construction": true});
            skLineSegment(sketch, "E91", {"start": v(-14.2, -14.24) * mm, "end": v(-44.5, -14.24) * mm});
            skLineSegment(sketch, "E92", {"start": v(-44.5, -14.24) * mm, "end": v(-44.5, -44.54) * mm});
            skLineSegment(sketch, "E93", {"start": v(-44.5, -44.54) * mm, "end": v(-22.64, -44.54) * mm});
            skLineSegment(sketch, "E94", {"start": v(-22.64, -44.54) * mm, "end": v(-20.25, -41.97) * mm});
            skLineSegment(sketch, "E95", {"start": v(-14.2, -14.24) * mm, "end": v(-14.2, -44.54) * mm});
            skLineSegment(sketch, "E96", {"start": v(-14.2, -44.54) * mm, "end": v(-18.55, -44.54) * mm});
            skLineSegment(sketch, "E97", {"start": v(-18.55, -44.54) * mm, "end": v(-16.65, -42.5) * mm});
            skArc(sketch, "E98", {"start": v(-16.65, -42.5) * mm, "mid": v(-17.84, -38.07) * mm, "end": v(-20.25, -41.97) * mm});
            skLineSegment(sketch, "E99", {"start": v(-14.2, -14.24) * mm, "end": v(-6.43, -14.24) * mm});
            skLineSegment(sketch, "E100", {"start": v(-6.43, -14.24) * mm, "end": v(-6.47, -44.54) * mm});
            skLineSegment(sketch, "E101", {"start": v(-14.2, -44.54) * mm, "end": v(-6.47, -44.54) * mm});
            skLineSegment(sketch, "E102", {"start": v(-6.47, -40.54) * mm, "end": v(-14.2, -40.54) * mm});
            skLineSegment(sketch, "E103.bottom", {"start": v(-29.35, -14.24) * mm, "end": v(-29.85, -14.24) * mm});
            skLineSegment(sketch, "E103.top", {"start": v(-29.35, -44.54) * mm, "end": v(-29.85, -44.54) * mm});
            skLineSegment(sketch, "E103.left", {"start": v(-29.35, -14.24) * mm, "end": v(-29.35, -21.25) * mm});
            skLineSegment(sketch, "E103.right", {"start": v(-29.85, -14.24) * mm, "end": v(-29.85, -21.26) * mm});
            skLineSegment(sketch, "E104", {"start": v(-29.85, -21.26) * mm, "end": v(-29.85, -35.55) * mm});
            skLineSegment(sketch, "E105", {"start": v(-29.35, -21.25) * mm, "end": v(-29.35, -37.54) * mm});
            skArc(sketch, "E106", {"start": v(-29.35, -23.24) * mm, "mid": v(-29.6, -23.25) * mm, "end": v(-29.85, -23.26) * mm});
            skArc(sketch, "E107", {"start": v(-29.85, -23.26) * mm, "mid": v(-35.5, -29.64) * mm, "end": v(-29.35, -35.54) * mm});
            skArc(sketch, "E108", {"start": v(-29.35, -35.54) * mm, "mid": v(-23.2, -29.4) * mm, "end": v(-29.35, -23.24) * mm});
            skLineSegment(sketch, "E109", {"start": v(-29.85, -35.55) * mm, "end": v(-29.85, -37.5) * mm});
            skLineSegment(sketch, "E110", {"start": v(-29.35, -37.54) * mm, "end": v(-29.35, -40.54) * mm});
            skLineSegment(sketch, "E111", {"start": v(-29.85, -37.5) * mm, "end": v(-29.85, -40.51) * mm});
            skLineSegment(sketch, "E112", {"start": v(-29.35, -40.54) * mm, "end": v(-29.35, -44.54) * mm});
            skLineSegment(sketch, "E113", {"start": v(-29.85, -40.51) * mm, "end": v(-29.85, -44.54) * mm});
            skArc(sketch, "E114", {"start": v(-29.86, -18.25) * mm, "mid": v(-29.1, -40.54) * mm, "end": v(-29.35, -18.24) * mm});
            skArc(sketch, "E115", {"start": v(-29.35, -18.24) * mm, "mid": v(-29.6, -18.24) * mm, "end": v(-29.86, -18.25) * mm});
            skSolve(sketch);
        }
        {
            var Q0;
            {var subQ0=sQuery(id+"F25.wireOp",EDGE,"E99");Q0=makeQuery(id+"F25.imprint","IMPRINT",FACE,{"disambiguationData":[TD([[makeQuery(id+"F25.imprint","IMPRINT",EDGE,{"derivedFrom":subQ0}),-1.0]])]});}
            var Q1;
            {var subQ0=sQuery(id+"F25.wireOp",EDGE,"E92");Q1=makeQuery(id+"F25.imprint","IMPRINT",FACE,{"disambiguationData":[TD([[makeQuery(id+"F25.imprint","IMPRINT",EDGE,{"derivedFrom":subQ0}),1.0]])]});}
            var Q2;
            {var subQ10=sQuery(id+"F25.wireOp",EDGE,"E94");Q2=makeQuery(id+"F25.imprint","IMPRINT",FACE,{"disambiguationData":[TD([[makeQuery(id+"F25.imprint","IMPRINT",EDGE,{"derivedFrom":subQ10}),1.0]])]});}
            var Q3;
            {var subQ0=sQuery(id+"F25.wireOp",EDGE,"E110");Q3=makeQuery(id+"F25.imprint","IMPRINT",FACE,{"disambiguationData":[TD([[makeQuery(id+"F25.imprint","IMPRINT",EDGE,{"derivedFrom":subQ0}),1.0]])]});}
            var Q4;
            {var subQ0=sQuery(id+"F25.wireOp",EDGE,"E113");var subQ1=sQuery(id+"F25.wireOp",EDGE,"E111");var subQ2=makeQuery(id+"F25.imprint","INTERSECT",VERTEX,{"derivedFrom":[subQ1,subQ0]});Q4=makeQuery(id+"F25.imprint","IMPRINT",FACE,{"disambiguationData":[TD([[makeQuery(id+"F25.imprint","IMPRINT",EDGE,{"disambiguationData":[TD([[subQ2,1.0]])],"derivedFrom":subQ1}),-1.0]])]});}
            var Q5;
            {var subQ0=sQuery(id+"F25.wireOp",EDGE,"E103.bottom");Q5=makeQuery(id+"F25.imprint","IMPRINT",FACE,{"disambiguationData":[TD([[makeQuery(id+"F25.imprint","IMPRINT",EDGE,{"derivedFrom":subQ0}),1.0]])]});}
            var Q6;
            {var subQ1=sQuery(id+"F25.wireOp",EDGE,"E78");var subQ3=sQuery(id+"F25.wireOp",EDGE,"E103.left");var subQ4=makeQuery(id+"F25.imprint","INTERSECT",VERTEX,{"derivedFrom":[subQ1,subQ3]});Q6=makeQuery(id+"F25.imprint","IMPRINT",FACE,{"disambiguationData":[TD([[makeQuery(id+"F25.imprint","IMPRINT",EDGE,{"disambiguationData":[TD([[subQ4,-1.0]])],"derivedFrom":subQ1}),-1.0]])]});}
            var Q7;
            {var subQ7=sQuery(id+"F25.wireOp",EDGE,"E110");Q7=makeQuery(id+"F25.imprint","IMPRINT",FACE,{"disambiguationData":[TD([[makeQuery(id+"F25.imprint","IMPRINT",EDGE,{"derivedFrom":subQ7}),-1.0]])]});}
            var Q8;
            {var subQ0=sQuery(id+"F25.wireOp",EDGE,"E103.top");Q8=makeQuery(id+"F25.imprint","IMPRINT",FACE,{"disambiguationData":[TD([[makeQuery(id+"F25.imprint","IMPRINT",EDGE,{"derivedFrom":subQ0}),-1.0]])]});}
            var Q9;
            {var subQ0=sQuery(id+"F25.wireOp",EDGE,"E101");Q9=makeQuery(id+"F25.imprint","IMPRINT",FACE,{"disambiguationData":[TD([[makeQuery(id+"F25.imprint","IMPRINT",EDGE,{"derivedFrom":subQ0}),1.0]])]});}
            extrude(context, id + "F26", {"entities" : qUnion([Q0, Q1, Q2, Q3, Q4, Q5, Q6, Q7, Q8, Q9]), "depth" : (getVariable(context, 'partwidth')) * mm, "hasSecondDirection" : true, "secondDirectionOppositeDirection" : true, "secondDirectionDepth" : 2 * mm});
        }
        {
            var Q0;
            {var subQ3=sQuery(id+"F25.wireOp",EDGE,"E108");Q0=makeQuery(id+"F25.imprint","IMPRINT",FACE,{"disambiguationData":[TD([[makeQuery(id+"F25.imprint","IMPRINT",EDGE,{"derivedFrom":subQ3}),-1.0]])]});}
            var Q1;
            {var subQ5=sQuery(id+"F25.wireOp",EDGE,"E109");Q1=makeQuery(id+"F25.imprint","IMPRINT",FACE,{"disambiguationData":[TD([[makeQuery(id+"F25.imprint","IMPRINT",EDGE,{"derivedFrom":subQ5}),-1.0]])]});}
            extrude(context, id + "F27", {"entities" : qUnion([Q0, Q1]), "operationType" : NewBodyOperationType.ADD, "depth" : 6 * mm});
        }
        {
            var Q0;
            Q0=makeQuery(id+"F15.imprint","IMPRINT",FACE,{"disambiguationData":[TD([[makeQuery(id+"F15.imprint","IMPRINT",EDGE,{"derivedFrom":sQuery(id+"F15.wireOp",EDGE,"E66.0")}),1.0]])]});
            extrude(context, id + "F28", {"entities" : qUnion([Q0]), "operationType" : NewBodyOperationType.REMOVE, "depth" : 50 * mm});
        }
        {
            var Q0;
            {var subQ9=sQuery(id+"F25.wireOp",EDGE,"E109");Q0=makeQuery(id+"F25.imprint","IMPRINT",FACE,{"disambiguationData":[TD([[makeQuery(id+"F25.imprint","IMPRINT",EDGE,{"derivedFrom":subQ9}),1.0]])]});}
            var Q1;
            {var subQ7=sQuery(id+"F25.wireOp",EDGE,"E110");Q1=makeQuery(id+"F25.imprint","IMPRINT",FACE,{"disambiguationData":[TD([[makeQuery(id+"F25.imprint","IMPRINT",EDGE,{"derivedFrom":subQ7}),-1.0]])]});}
            var Q2;
            {var subQ0=sQuery(id+"F25.wireOp",EDGE,"E103.top");Q2=makeQuery(id+"F25.imprint","IMPRINT",FACE,{"disambiguationData":[TD([[makeQuery(id+"F25.imprint","IMPRINT",EDGE,{"derivedFrom":subQ0}),-1.0]])]});}
            var Q3;
            {var subQ3=sQuery(id+"F25.wireOp",EDGE,"E106");Q3=makeQuery(id+"F25.imprint","IMPRINT",FACE,{"disambiguationData":[TD([[makeQuery(id+"F25.imprint","IMPRINT",EDGE,{"derivedFrom":subQ3}),-1.0]])]});}
            var Q4;
            {var subQ1=sQuery(id+"F25.wireOp",EDGE,"E78");var subQ3=sQuery(id+"F25.wireOp",EDGE,"E103.left");var subQ4=makeQuery(id+"F25.imprint","INTERSECT",VERTEX,{"derivedFrom":[subQ1,subQ3]});Q4=makeQuery(id+"F25.imprint","IMPRINT",FACE,{"disambiguationData":[TD([[makeQuery(id+"F25.imprint","IMPRINT",EDGE,{"disambiguationData":[TD([[subQ4,-1.0]])],"derivedFrom":subQ1}),-1.0]])]});}
            var Q5;
            {var subQ0=sQuery(id+"F25.wireOp",EDGE,"E103.bottom");Q5=makeQuery(id+"F25.imprint","IMPRINT",FACE,{"disambiguationData":[TD([[makeQuery(id+"F25.imprint","IMPRINT",EDGE,{"derivedFrom":subQ0}),1.0]])]});}
            extrude(context, id + "F29", {"entities" : qUnion([Q0, Q1, Q2, Q3, Q4, Q5]), "operationType" : NewBodyOperationType.REMOVE, "endBound" : BoundingType.SYMMETRIC, "oppositeDirection" : true, "depth" : 25 * mm});
        }
        {
            var Q0;
            Q0=makeQuery(id+"F29.boolean.opBoolean","SPLIT",BODY,{"disambiguationData":[OD(1.0)],"derivedFrom":makeQuery(id+"F26.opExtrude","SWEPT_BODY",BODY,{"disambiguationData":[OSD([sQuery(id+"F25.wireOp",EDGE,"E78"),sQuery(id+"F25.wireOp",EDGE,"E91"),sQuery(id+"F25.wireOp",EDGE,"E92"),sQuery(id+"F25.wireOp",EDGE,"E93"),sQuery(id+"F25.wireOp",EDGE,"E94"),sQuery(id+"F25.wireOp",EDGE,"E95"),sQuery(id+"F25.wireOp",EDGE,"E96"),sQuery(id+"F25.wireOp",EDGE,"E97"),sQuery(id+"F25.wireOp",EDGE,"E98"),sQuery(id+"F25.wireOp",EDGE,"E99"),sQuery(id+"F25.wireOp",EDGE,"E100"),sQuery(id+"F25.wireOp",EDGE,"E102"),sQuery(id+"F25.wireOp",EDGE,"E103.bottom"),sQuery(id+"F25.wireOp",EDGE,"E103.top")])]})});
            var Q1;
            Q1=makeQuery(id+"F11.opPattern","COPY",BODY,{"derivedFrom":makeQuery(id+"F4.opExtrude","SWEPT_BODY",BODY,{"disambiguationData":[OSD([sQuery(id+"F3.wireOp",EDGE,"E5.0"),sQuery(id+"F3.wireOp",EDGE,"E5.1"),sQuery(id+"F3.wireOp",EDGE,"E5.2"),sQuery(id+"F3.wireOp",EDGE,"E5.3"),sQuery(id+"F3.wireOp",EDGE,"E5.4"),sQuery(id+"F3.wireOp",EDGE,"E5.5"),sQuery(id+"F3.wireOp",EDGE,"E29"),sQuery(id+"F3.wireOp",EDGE,"E30"),sQuery(id+"F3.wireOp",EDGE,"E31"),sQuery(id+"F3.wireOp",EDGE,"E33"),sQuery(id+"F3.wireOp",EDGE,"E35"),sQuery(id+"F3.wireOp",EDGE,"E36.trimOffspring"),sQuery(id+"F3.wireOp",EDGE,"E37"),sQuery(id+"F3.wireOp",EDGE,"E40"),sQuery(id+"F3.wireOp",EDGE,"E41"),sQuery(id+"F3.wireOp",EDGE,"E44"),sQuery(id+"F3.wireOp",EDGE,"E49"),sQuery(id+"F3.wireOp",EDGE,"E50"),sQuery(id+"F3.wireOp",EDGE,"E51"),sQuery(id+"F3.wireOp",EDGE,"E53"),sQuery(id+"F3.wireOp",EDGE,"E54")])]}),"instanceName":"1"});
            booleanBodies(context, id + "F30", {"operationType" : BooleanOperationType.UNION, "tools" : qUnion([Q0, Q1])});
        }
        {
            var Q0;
            {var subQ2=sQuery(id+"F25.wireOp",EDGE,"E100");var subQ3=sQuery(id+"F25.wireOp",EDGE,"E98");var subQ4=sQuery(id+"F25.wireOp",EDGE,"E101");var subQ5=sQuery(id+"F25.wireOp",EDGE,"E96");var subQ6=sQuery(id+"F25.wireOp",EDGE,"E78");var subQ7=sQuery(id+"F25.wireOp",EDGE,"E103.top");var subQ8=sQuery(id+"F25.wireOp",EDGE,"E93");var subQ9=sQuery(id+"F25.wireOp",EDGE,"E103.bottom");var subQ10=sQuery(id+"F25.wireOp",EDGE,"E99");var subQ11=sQuery(id+"F25.wireOp",EDGE,"E91");var subQ12=sQuery(id+"F25.wireOp",EDGE,"E97");var subQ13=sQuery(id+"F25.wireOp",EDGE,"E94");var subQ14=makeQuery(id+"F4.opExtrude","CAP_FACE",FACE,{"disambiguationData":[OSD([sQuery(id+"F3.wireOp",EDGE,"E5.0"),sQuery(id+"F3.wireOp",EDGE,"E5.1"),sQuery(id+"F3.wireOp",EDGE,"E5.2"),sQuery(id+"F3.wireOp",EDGE,"E5.3"),sQuery(id+"F3.wireOp",EDGE,"E5.4"),sQuery(id+"F3.wireOp",EDGE,"E5.5"),sQuery(id+"F3.wireOp",EDGE,"E29"),sQuery(id+"F3.wireOp",EDGE,"E30"),sQuery(id+"F3.wireOp",EDGE,"E31"),sQuery(id+"F3.wireOp",EDGE,"E33"),sQuery(id+"F3.wireOp",EDGE,"E35"),sQuery(id+"F3.wireOp",EDGE,"E36.trimOffspring"),sQuery(id+"F3.wireOp",EDGE,"E37"),sQuery(id+"F3.wireOp",EDGE,"E40"),sQuery(id+"F3.wireOp",EDGE,"E41"),sQuery(id+"F3.wireOp",EDGE,"E44"),sQuery(id+"F3.wireOp",EDGE,"E49"),sQuery(id+"F3.wireOp",EDGE,"E50"),sQuery(id+"F3.wireOp",EDGE,"E51"),sQuery(id+"F3.wireOp",EDGE,"E53"),sQuery(id+"F3.wireOp",EDGE,"E54")])],"isStart":false});Q0=makeQuery(id+"F30.opBoolean","INTERSECT",EDGE,{"derivedFrom":[makeQuery(id+"F11.opPattern","COPY",FACE,{"derivedFrom":makeQuery(id+"F7.boolean.opBoolean","MERGE",FACE,{"derivedFrom":[subQ14,makeQuery(id+"F7.opPattern","COPY",FACE,{"derivedFrom":subQ14,"instanceName":"1"})]}),"instanceName":"1"}),makeQuery(id+"F29.boolean.opBoolean","SPLIT",FACE,{"disambiguationData":[TD([makeQuery(id+"F26.opExtrude","SWEPT_FACE",FACE,{"disambiguationData":[OSD([subQ13])]})])],"derivedFrom":makeQuery(id+"F26.opExtrude","CAP_FACE",FACE,{"disambiguationData":[OSD([subQ6,subQ11,sQuery(id+"F25.wireOp",EDGE,"E92"),subQ8,subQ13,subQ5,subQ12,subQ3,subQ10,subQ2,subQ4,subQ9,subQ7])],"isStart":false})})]});}
            fillet(context, id + "F31", {"entities" : qUnion([Q0]), "radius" : 5 * mm, "tangentPropagation" : true, "allowEdgeOverflow" : false});
        }
        {
            var Q0;
            {var subQ2=sQuery(id+"F25.wireOp",EDGE,"E98");var subQ3=sQuery(id+"F25.wireOp",EDGE,"E101");var subQ4=sQuery(id+"F25.wireOp",EDGE,"E96");var subQ5=sQuery(id+"F25.wireOp",EDGE,"E78");var subQ6=sQuery(id+"F25.wireOp",EDGE,"E103.top");var subQ7=sQuery(id+"F25.wireOp",EDGE,"E93");var subQ8=sQuery(id+"F25.wireOp",EDGE,"E103.bottom");var subQ9=sQuery(id+"F25.wireOp",EDGE,"E99");var subQ10=sQuery(id+"F25.wireOp",EDGE,"E91");var subQ11=sQuery(id+"F25.wireOp",EDGE,"E97");var subQ12=sQuery(id+"F25.wireOp",EDGE,"E94");var subQ13=makeQuery(id+"F4.opExtrude","CAP_FACE",FACE,{"disambiguationData":[OSD([sQuery(id+"F3.wireOp",EDGE,"E5.0"),sQuery(id+"F3.wireOp",EDGE,"E5.1"),sQuery(id+"F3.wireOp",EDGE,"E5.2"),sQuery(id+"F3.wireOp",EDGE,"E5.3"),sQuery(id+"F3.wireOp",EDGE,"E5.4"),sQuery(id+"F3.wireOp",EDGE,"E5.5"),sQuery(id+"F3.wireOp",EDGE,"E29"),sQuery(id+"F3.wireOp",EDGE,"E30"),sQuery(id+"F3.wireOp",EDGE,"E31"),sQuery(id+"F3.wireOp",EDGE,"E33"),sQuery(id+"F3.wireOp",EDGE,"E35"),sQuery(id+"F3.wireOp",EDGE,"E36.trimOffspring"),sQuery(id+"F3.wireOp",EDGE,"E37"),sQuery(id+"F3.wireOp",EDGE,"E40"),sQuery(id+"F3.wireOp",EDGE,"E41"),sQuery(id+"F3.wireOp",EDGE,"E44"),sQuery(id+"F3.wireOp",EDGE,"E49"),sQuery(id+"F3.wireOp",EDGE,"E50"),sQuery(id+"F3.wireOp",EDGE,"E51"),sQuery(id+"F3.wireOp",EDGE,"E53"),sQuery(id+"F3.wireOp",EDGE,"E54")])],"isStart":false});Q0=makeQuery(id+"F30.opBoolean","INTERSECT",EDGE,{"derivedFrom":[makeQuery(id+"F11.opPattern","COPY",FACE,{"derivedFrom":makeQuery(id+"F7.boolean.opBoolean","MERGE",FACE,{"derivedFrom":[subQ13,makeQuery(id+"F7.opPattern","COPY",FACE,{"derivedFrom":subQ13,"instanceName":"1"})]}),"instanceName":"1"}),makeQuery(id+"F29.boolean.opBoolean","SPLIT",FACE,{"disambiguationData":[TD([makeQuery(id+"F26.opExtrude","SWEPT_FACE",FACE,{"disambiguationData":[OSD([subQ12])]})])],"derivedFrom":makeQuery(id+"F26.opExtrude","CAP_FACE",FACE,{"disambiguationData":[OSD([subQ5,subQ10,sQuery(id+"F25.wireOp",EDGE,"E92"),subQ7,subQ12,subQ4,subQ11,subQ2,subQ9,sQuery(id+"F25.wireOp",EDGE,"E100"),subQ3,subQ8,subQ6])],"isStart":true})})]});}
            fillet(context, id + "F32", {"entities" : qUnion([Q0]), "radius" : 5 * mm, "tangentPropagation" : true, "allowEdgeOverflow" : false});
        }
        {
            var Q0;
            Q0=makeQuery(id+"F26.opExtrude","SWEPT_EDGE",EDGE,{"disambiguationData":[OSD([sQuery(id+"F25.wireOp",EDGE,"E92"),sQuery(id+"F25.wireOp",EDGE,"E93")])]});
            var Q1;
            Q1=makeQuery(id+"F26.opExtrude","SWEPT_EDGE",EDGE,{"disambiguationData":[OSD([sQuery(id+"F25.wireOp",EDGE,"E91"),sQuery(id+"F25.wireOp",EDGE,"E92")])]});
            fillet(context, id + "F33", {"entities" : qUnion([Q0, Q1]), "radius" : 5 * mm, "tangentPropagation" : true, "allowEdgeOverflow" : false});
        }
        {
            var Q0;
            Q0=makeQuery(id+"F26.opExtrude","SWEPT_EDGE",EDGE,{"disambiguationData":[OSD([sQuery(id+"F25.wireOp",EDGE,"E100"),sQuery(id+"F25.wireOp",EDGE,"E101")])]});
            fillet(context, id + "F34", {"entities" : qUnion([Q0]), "radius" : 5 * mm, "tangentPropagation" : true, "allowEdgeOverflow" : false});
        }
        {
            var Q0;
            Q0=makeQuery(id+"F26.opExtrude","SWEPT_FACE",FACE,{"disambiguationData":[OSD([sQuery(id+"F25.wireOp",EDGE,"E92")])]});
            var sketch = newSketch(context, id + "F35", { "sketchPlane" : qUnion([Q0])});
            skLineSegment(sketch, "E116.0.0", {"start": v(39.54, 8) * mm, "end": v(19.24, 8) * mm});
            skLineSegment(sketch, "E116.0.1", {"start": v(19.24, 8) * mm, "end": v(19.24, -2) * mm});
            skLineSegment(sketch, "E116.0.2", {"start": v(19.24, -2) * mm, "end": v(39.54, -2) * mm});
            skLineSegment(sketch, "E116.0.3", {"start": v(39.54, -2) * mm, "end": v(39.54, 8) * mm});
            skCircle(sketch, "E117", {"center": v(19.24, 3) * mm, "radius": 1.6 * mm});
            skCircle(sketch, "E118", {"center": v(39.54, 3) * mm, "radius": 1.6 * mm});
            skSolve(sketch);
        }
        {
            var Q0;
            Q0=sQuery(id+"F35.wireOp",VERTEX,"E117.center");
            var Q1;
            Q1=sQuery(id+"F35.wireOp",VERTEX,"E118.center");
            var Q2;
            Q2=makeQuery(id+"F29.boolean.opBoolean","SPLIT",BODY,{"disambiguationData":[OD(0.0)],"derivedFrom":makeQuery(id+"F26.opExtrude","SWEPT_BODY",BODY,{"disambiguationData":[OSD([sQuery(id+"F25.wireOp",EDGE,"E78"),sQuery(id+"F25.wireOp",EDGE,"E91"),sQuery(id+"F25.wireOp",EDGE,"E92"),sQuery(id+"F25.wireOp",EDGE,"E93"),sQuery(id+"F25.wireOp",EDGE,"E94"),sQuery(id+"F25.wireOp",EDGE,"E96"),sQuery(id+"F25.wireOp",EDGE,"E97"),sQuery(id+"F25.wireOp",EDGE,"E98"),sQuery(id+"F25.wireOp",EDGE,"E99"),sQuery(id+"F25.wireOp",EDGE,"E100"),sQuery(id+"F25.wireOp",EDGE,"E101"),sQuery(id+"F25.wireOp",EDGE,"E103.bottom"),sQuery(id+"F25.wireOp",EDGE,"E103.top")])]})});
            var Q3;
            Q3=makeQuery(id+"F29.boolean.opBoolean","SPLIT",BODY,{"disambiguationData":[OD(1.0)],"derivedFrom":makeQuery(id+"F26.opExtrude","SWEPT_BODY",BODY,{"disambiguationData":[OSD([sQuery(id+"F25.wireOp",EDGE,"E78"),sQuery(id+"F25.wireOp",EDGE,"E91"),sQuery(id+"F25.wireOp",EDGE,"E92"),sQuery(id+"F25.wireOp",EDGE,"E93"),sQuery(id+"F25.wireOp",EDGE,"E94"),sQuery(id+"F25.wireOp",EDGE,"E96"),sQuery(id+"F25.wireOp",EDGE,"E97"),sQuery(id+"F25.wireOp",EDGE,"E98"),sQuery(id+"F25.wireOp",EDGE,"E99"),sQuery(id+"F25.wireOp",EDGE,"E100"),sQuery(id+"F25.wireOp",EDGE,"E101"),sQuery(id+"F25.wireOp",EDGE,"E103.bottom"),sQuery(id+"F25.wireOp",EDGE,"E103.top")])]})});
            hole(context, id + "F36", {"style" : HoleStyle.C_BORE, "endStyle" : HoleEndStyle.BLIND_IN_LAST, "holeDiameter" : 3.2 * mm, "cBoreDiameter" : 6.2 * mm, "cBoreDepth" : 3 * mm, "tapDrillDiameter" : 3.2 * mm, "holeDepth" : 7 * mm, "startFromSketch" : true, "locations" : qUnion([Q0, Q1]), "scope" : qUnion([Q2, Q3])});
        }
        {
            var Q0;
            Q0=makeQuery(id+"F20.opPattern","COPY",FACE,{"derivedFrom":makeQuery(id+"F11.opPattern","COPY",FACE,{"derivedFrom":makeQuery(id+"F5.opExtrude","CAP_FACE",FACE,{"disambiguationData":[OSD([sQuery(id+"F3.wireOp",EDGE,"E4"),sQuery(id+"F3.wireOp",EDGE,"E5.0"),sQuery(id+"F3.wireOp",EDGE,"E5.1"),sQuery(id+"F3.wireOp",EDGE,"E5.2"),sQuery(id+"F3.wireOp",EDGE,"E5.3"),sQuery(id+"F3.wireOp",EDGE,"E5.4"),sQuery(id+"F3.wireOp",EDGE,"E5.5")])],"isStart":false}),"instanceName":"1"}),"instanceName":"1"});
            extrude(context, id + "F37", {"entities" : qUnion([Q0]), "operationType" : NewBodyOperationType.ADD, "depth" : 3 * mm});
        }
        {
            var Q0;
            Q0=makeQuery(id+"F20.opPattern","COPY",FACE,{"derivedFrom":makeQuery(id+"F11.opPattern","COPY",FACE,{"derivedFrom":makeQuery(id+"F7.opPattern","COPY",FACE,{"derivedFrom":makeQuery(id+"F5.opExtrude","CAP_FACE",FACE,{"disambiguationData":[OSD([sQuery(id+"F3.wireOp",EDGE,"E4"),sQuery(id+"F3.wireOp",EDGE,"E5.0"),sQuery(id+"F3.wireOp",EDGE,"E5.1"),sQuery(id+"F3.wireOp",EDGE,"E5.2"),sQuery(id+"F3.wireOp",EDGE,"E5.3"),sQuery(id+"F3.wireOp",EDGE,"E5.4"),sQuery(id+"F3.wireOp",EDGE,"E5.5")])],"isStart":false}),"instanceName":"1"}),"instanceName":"1"}),"instanceName":"1"});
            extrude(context, id + "F38", {"entities" : qUnion([Q0]), "operationType" : NewBodyOperationType.ADD, "depth" : 3 * mm});
        }
        {
            var Q0;
            Q0=makeQuery(id+"F17.opPattern","COPY",FACE,{"derivedFrom":makeQuery(id+"F7.opPattern","COPY",FACE,{"derivedFrom":makeQuery(id+"F5.opExtrude","CAP_FACE",FACE,{"disambiguationData":[OSD([sQuery(id+"F3.wireOp",EDGE,"E4"),sQuery(id+"F3.wireOp",EDGE,"E5.0"),sQuery(id+"F3.wireOp",EDGE,"E5.1"),sQuery(id+"F3.wireOp",EDGE,"E5.2"),sQuery(id+"F3.wireOp",EDGE,"E5.3"),sQuery(id+"F3.wireOp",EDGE,"E5.4"),sQuery(id+"F3.wireOp",EDGE,"E5.5")])],"isStart":false}),"instanceName":"1"}),"instanceName":"1"});
            extrude(context, id + "F39", {"entities" : qUnion([Q0]), "operationType" : NewBodyOperationType.ADD, "depth" : 3 * mm});
        }
        {
            var Q0;
            Q0=makeQuery(id+"F17.opPattern","COPY",FACE,{"derivedFrom":makeQuery(id+"F5.opExtrude","CAP_FACE",FACE,{"disambiguationData":[OSD([sQuery(id+"F3.wireOp",EDGE,"E4"),sQuery(id+"F3.wireOp",EDGE,"E5.0"),sQuery(id+"F3.wireOp",EDGE,"E5.1"),sQuery(id+"F3.wireOp",EDGE,"E5.2"),sQuery(id+"F3.wireOp",EDGE,"E5.3"),sQuery(id+"F3.wireOp",EDGE,"E5.4"),sQuery(id+"F3.wireOp",EDGE,"E5.5")])],"isStart":false}),"instanceName":"1"});
            extrude(context, id + "F40", {"entities" : qUnion([Q0]), "operationType" : NewBodyOperationType.ADD, "depth" : 3 * mm});
        }
    });
